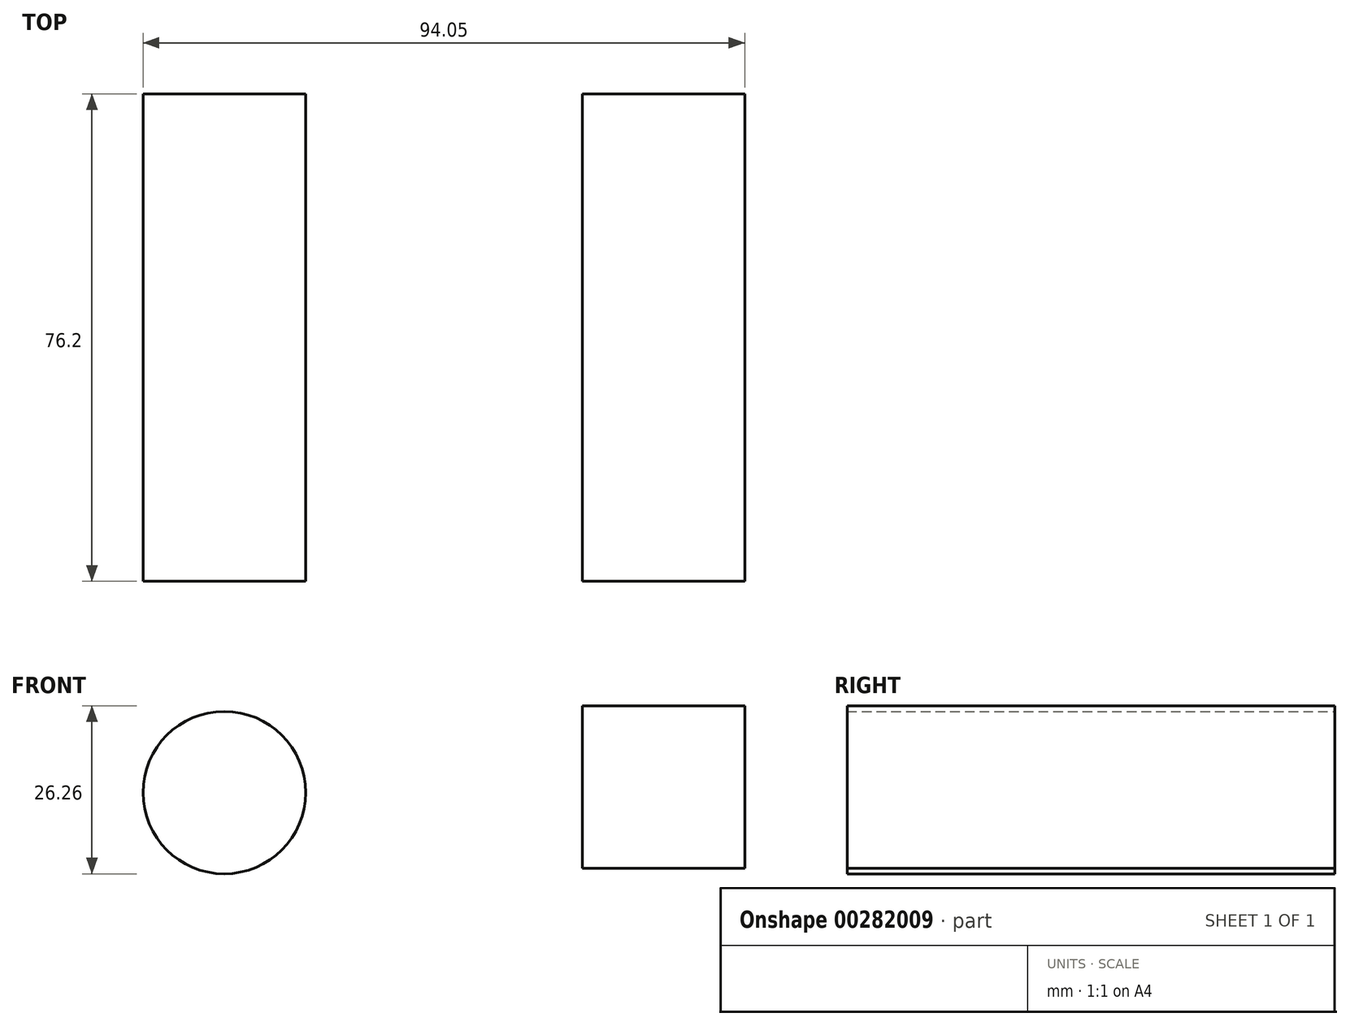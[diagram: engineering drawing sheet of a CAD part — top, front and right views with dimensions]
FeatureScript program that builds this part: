
annotation { "Feature Type Name" : "Feature", "Feature Type Description" : "" }
export const myFeature = defineFeature(function(context is Context, id is Id, definition is map)
    precondition{}
    {
        {
            var Q0;
            Q0=qCreatedBy(makeId("Front.planeOp"),FACE);
            var sketch = newSketch(context, id + "F0", { "sketchPlane" : qUnion([Q0])});
            skCircle(sketch, "E0", {"center": v(-47.93, 28.26) * mm, "radius": 12.7 * mm});
            skLineSegment(sketch, "E1.bottom", {"start": v(33.42, 16.42) * mm, "end": v(8.02, 16.42) * mm});
            skLineSegment(sketch, "E1.top", {"start": v(33.42, 41.82) * mm, "end": v(8.02, 41.82) * mm});
            skLineSegment(sketch, "E1.left", {"start": v(33.42, 16.42) * mm, "end": v(33.42, 41.82) * mm});
            skLineSegment(sketch, "E1.right", {"start": v(8.02, 16.42) * mm, "end": v(8.02, 41.82) * mm});
            skSolve(sketch);
        }
        {
            var Q0;
            Q0 = qSketchRegion(id + "F0", true);
            extrude(context, id + "F1", {"entities" : qUnion([Q0]), "depth" : 76.2 * mm});
        }
    });
